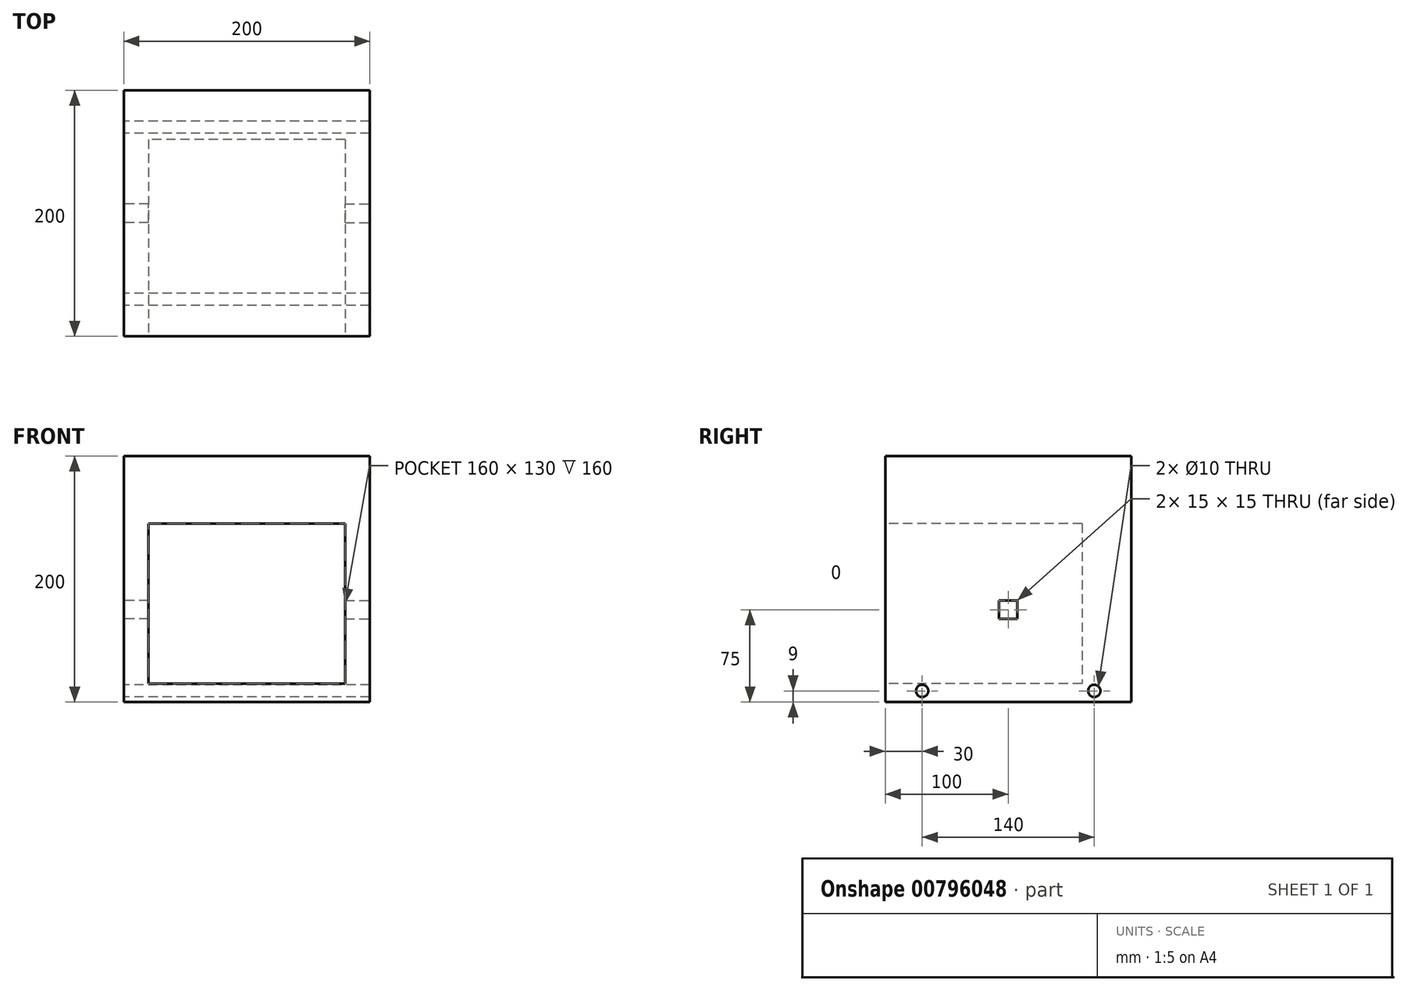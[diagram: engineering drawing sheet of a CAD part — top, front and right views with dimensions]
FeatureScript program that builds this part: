
annotation { "Feature Type Name" : "Feature", "Feature Type Description" : "" }
export const myFeature = defineFeature(function(context is Context, id is Id, definition is map)
    precondition{}
    {
        {
            var Q0;
            Q0=qCreatedBy(makeId("Top.planeOp"),FACE);
            var sketch = newSketch(context, id + "F0", { "sketchPlane" : qUnion([Q0])});
            skLineSegment(sketch, "E0.bottom", {"start": v(100, -100) * mm, "end": v(-100, -100) * mm});
            skLineSegment(sketch, "E0.top", {"start": v(100, 100) * mm, "end": v(-100, 100) * mm});
            skLineSegment(sketch, "E0.left", {"start": v(100, -100) * mm, "end": v(100, 100) * mm});
            skLineSegment(sketch, "E0.right", {"start": v(-100, -100) * mm, "end": v(-100, 100) * mm});
            skPoint(sketch, "E0.middle", {"position": v(0, 0) * mm});
            skSolve(sketch);
        }
        {
            var Q0;
            Q0=makeQuery(id+"F0.imprint","IMPRINT",FACE,{"disambiguationData":[TD([[makeQuery(id+"F0.imprint","IMPRINT",EDGE,{"derivedFrom":sQuery(id+"F0.wireOp",EDGE,"E0.bottom")}),-1.0]])]});
            extrude(context, id + "F1", {"entities" : qUnion([Q0]), "depth" : 200 * mm, "offsetDistance" : 25 * mm});
        }
        {
            var Q0;
            Q0=makeQuery(id+"F1.opExtrude","SWEPT_FACE",FACE,{"disambiguationData":[OSD([sQuery(id+"F0.wireOp",EDGE,"E0.bottom")])]});
            var sketch = newSketch(context, id + "F2", { "sketchPlane" : qUnion([Q0])});
            skLineSegment(sketch, "E1.bottom", {"start": v(80, 145) * mm, "end": v(-80, 145) * mm});
            skLineSegment(sketch, "E1.top", {"start": v(80, 15) * mm, "end": v(-80, 15) * mm});
            skLineSegment(sketch, "E1.left", {"start": v(80, 145) * mm, "end": v(80, 15) * mm});
            skLineSegment(sketch, "E1.right", {"start": v(-80, 145) * mm, "end": v(-80, 15) * mm});
            skPoint(sketch, "E1.middle", {"position": v(0, 80) * mm});
            skSolve(sketch);
        }
        {
            var Q0;
            Q0=makeQuery(id+"F2.imprint","IMPRINT",FACE,{"disambiguationData":[TD([[makeQuery(id+"F2.imprint","IMPRINT",EDGE,{"derivedFrom":sQuery(id+"F2.wireOp",EDGE,"E1.bottom")}),1.0]])]});
            extrude(context, id + "F3", {"entities" : qUnion([Q0]), "operationType" : NewBodyOperationType.REMOVE, "oppositeDirection" : true, "depth" : 160 * mm, "offsetDistance" : 25 * mm});
        }
        {
            var Q0;
            Q0=makeQuery(id+"F1.opExtrude","SWEPT_FACE",FACE,{"disambiguationData":[OSD([sQuery(id+"F0.wireOp",EDGE,"E0.left")])]});
            var sketch = newSketch(context, id + "F4", { "sketchPlane" : qUnion([Q0])});
            skLineSegment(sketch, "E2", {"start": v(-100, 0) * mm, "end": v(0, 0) * mm});
            skLineSegment(sketch, "E3", {"start": v(0, 0) * mm, "end": v(0, 75) * mm});
            skLineSegment(sketch, "E4.bottom", {"start": v(7.5, 67.5) * mm, "end": v(-7.5, 67.5) * mm});
            skLineSegment(sketch, "E4.top", {"start": v(7.5, 82.5) * mm, "end": v(-7.5, 82.5) * mm});
            skLineSegment(sketch, "E4.left", {"start": v(7.5, 67.5) * mm, "end": v(7.5, 82.5) * mm});
            skLineSegment(sketch, "E4.right", {"start": v(-7.5, 67.5) * mm, "end": v(-7.5, 82.5) * mm});
            skPoint(sketch, "E4.middle", {"position": v(0, 75) * mm});
            skSolve(sketch);
        }
        {
            var Q0;
            Q0=makeQuery(id+"F4.imprint","IMPRINT",FACE,{"disambiguationData":[TD([[makeQuery(id+"F4.imprint","IMPRINT",EDGE,{"derivedFrom":sQuery(id+"F4.wireOp",EDGE,"E4.top")}),1.0]])]});
            extrude(context, id + "F5", {"entities" : qUnion([Q0]), "operationType" : NewBodyOperationType.REMOVE, "oppositeDirection" : true, "depth" : 24 * mm, "offsetDistance" : 25 * mm});
        }
        {
            var Q0;
            Q0=makeQuery(id+"F1.opExtrude","SWEPT_FACE",FACE,{"disambiguationData":[OSD([sQuery(id+"F0.wireOp",EDGE,"E0.right")])]});
            var sketch = newSketch(context, id + "F6", { "sketchPlane" : qUnion([Q0])});
            skLineSegment(sketch, "E5", {"start": v(100, 0) * mm, "end": v(0, 0) * mm});
            skLineSegment(sketch, "E6", {"start": v(0, 0) * mm, "end": v(0, 75) * mm});
            skLineSegment(sketch, "E7.bottom", {"start": v(7.5, 67.5) * mm, "end": v(-7.5, 67.5) * mm});
            skLineSegment(sketch, "E7.top", {"start": v(7.5, 82.5) * mm, "end": v(-7.5, 82.5) * mm});
            skLineSegment(sketch, "E7.left", {"start": v(7.5, 67.5) * mm, "end": v(7.5, 82.5) * mm});
            skLineSegment(sketch, "E7.right", {"start": v(-7.5, 67.5) * mm, "end": v(-7.5, 82.5) * mm});
            skPoint(sketch, "E7.middle", {"position": v(0, 75) * mm});
            skSolve(sketch);
        }
        {
            var Q0;
            Q0=makeQuery(id+"F1.opExtrude","SWEPT_FACE",FACE,{"disambiguationData":[OSD([sQuery(id+"F0.wireOp",EDGE,"E0.left")])]});
            var sketch = newSketch(context, id + "F7", { "sketchPlane" : qUnion([Q0])});
            skLineSegment(sketch, "E8.bottom", {"start": v(-100, 0) * mm, "end": v(-70, 0) * mm});
            skLineSegment(sketch, "E8.left", {"start": v(-100, 0) * mm, "end": v(-100, 9) * mm});
            skCircle(sketch, "E9", {"center": v(70, 9) * mm, "radius": 5 * mm});
            skCircle(sketch, "E10", {"center": v(-70, 9) * mm, "radius": 5 * mm});
            skSolve(sketch);
        }
        {
            var Q0;
            Q0=makeQuery(id+"F6.imprint","IMPRINT",FACE,{"disambiguationData":[TD([[makeQuery(id+"F6.imprint","IMPRINT",EDGE,{"derivedFrom":sQuery(id+"F6.wireOp",EDGE,"E7.top")}),1.0]])]});
            var Q1;
            Q1 = qSketchRegion(id + "F7", true);
            extrude(context, id + "F8", {"entities" : qUnion([Q0, Q1]), "operationType" : NewBodyOperationType.REMOVE, "oppositeDirection" : true, "depth" : 25 * mm, "offsetDistance" : 25 * mm});
        }
        {
            var Q0;
            Q0=makeQuery(id+"F7.imprint","IMPRINT",FACE,{"disambiguationData":[TD([[makeQuery(id+"F7.imprint","IMPRINT",EDGE,{"derivedFrom":sQuery(id+"F7.wireOp",EDGE,"E10")}),1.0]])]});
            var Q1;
            Q1=sQuery(id+"F7.wireOp",EDGE,"E10");
            extrude(context, id + "F9", {"entities" : qUnion([Q0]), "operationType" : NewBodyOperationType.REMOVE, "surfaceEntities" : qUnion([Q1]), "depth" : 25 * mm, "offsetDistance" : 25 * mm, "hasSecondDirection" : true, "secondDirectionOppositeDirection" : true, "secondDirectionDepth" : 203.2 * mm});
        }
        {
            var Q0;
            Q0=makeQuery(id+"F7.imprint","IMPRINT",FACE,{"disambiguationData":[TD([[makeQuery(id+"F7.imprint","IMPRINT",EDGE,{"derivedFrom":sQuery(id+"F7.wireOp",EDGE,"E9")}),1.0]])]});
            var Q1;
            Q1=sQuery(id+"F7.wireOp",EDGE,"E9");
            extrude(context, id + "F10", {"entities" : qUnion([Q0]), "operationType" : NewBodyOperationType.REMOVE, "surfaceEntities" : qUnion([Q1]), "depth" : 25 * mm, "offsetDistance" : 25 * mm, "hasSecondDirection" : true, "secondDirectionOppositeDirection" : true, "secondDirectionDepth" : 215.8 * mm});
        }
    });
